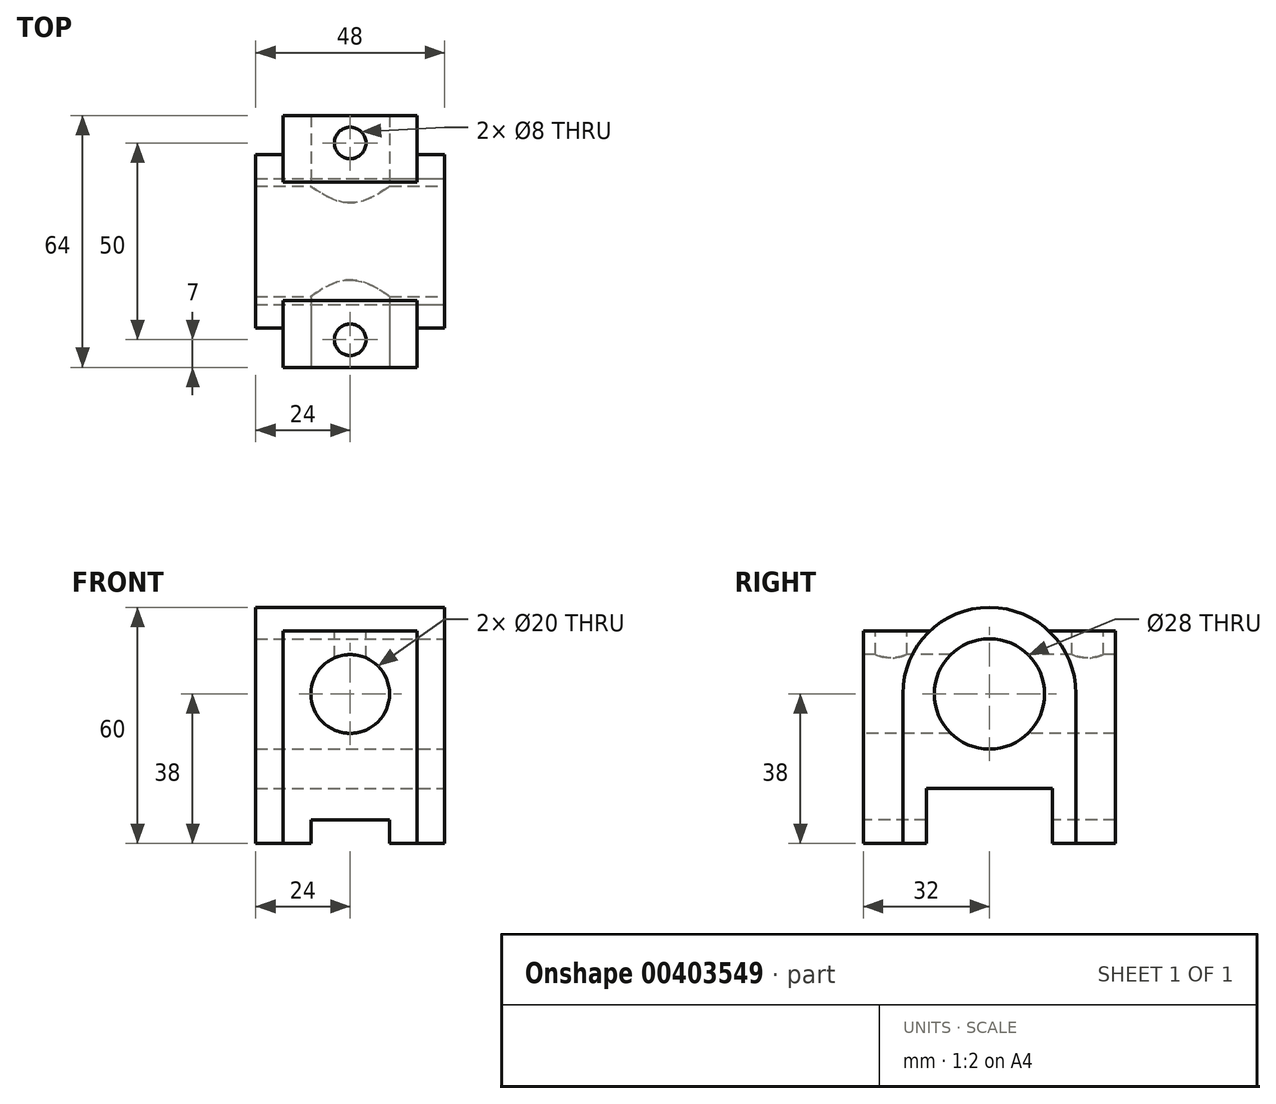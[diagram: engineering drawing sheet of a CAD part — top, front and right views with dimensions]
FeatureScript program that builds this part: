
annotation { "Feature Type Name" : "Feature", "Feature Type Description" : "" }
export const myFeature = defineFeature(function(context is Context, id is Id, definition is map)
    precondition{}
    {
        {
            var Q0;
            Q0=qCreatedBy(makeId("Right.planeOp"),FACE);
            var sketch = newSketch(context, id + "F0", { "sketchPlane" : qUnion([Q0])});
            skLineSegment(sketch, "E0.bottom", {"start": v(-22, 30) * mm, "end": v(22, 30) * mm});
            skLineSegment(sketch, "E0.top", {"start": v(-22, -30) * mm, "end": v(22, -30) * mm});
            skLineSegment(sketch, "E0.left", {"start": v(-22, 30) * mm, "end": v(-22, -30) * mm});
            skLineSegment(sketch, "E0.right", {"start": v(22, 30) * mm, "end": v(22, -30) * mm});
            skPoint(sketch, "E0.middle", {"position": v(0, 0) * mm});
            skSolve(sketch);
        }
        {
            var Q0;
            Q0 = qSketchRegion(id + "F0", true);
            extrude(context, id + "F1", {"entities" : qUnion([Q0]), "endBound" : BoundingType.SYMMETRIC, "depth" : 48 * mm});
        }
        {
            var Q0;
            Q0=makeQuery(id+"F1.opExtrude","SWEPT_EDGE",EDGE,{"disambiguationData":[OSD([sQuery(id+"F0.wireOp",EDGE,"E0.bottom"),sQuery(id+"F0.wireOp",EDGE,"E0.left")])]});
            var Q1;
            Q1=makeQuery(id+"F1.opExtrude","SWEPT_EDGE",EDGE,{"disambiguationData":[OSD([sQuery(id+"F0.wireOp",EDGE,"E0.bottom"),sQuery(id+"F0.wireOp",EDGE,"E0.right")])]});
            fillet(context, id + "F2", {"entities" : qUnion([Q0, Q1]), "radius" : 22 * mm, "tangentPropagation" : true, "allowEdgeOverflow" : false});
        }
        {
            var Q0;
            Q0=makeQuery(id+"F1.opExtrude","SWEPT_FACE",FACE,{"disambiguationData":[OSD([sQuery(id+"F0.wireOp",EDGE,"E0.left")])]});
            var sketch = newSketch(context, id + "F3", { "sketchPlane" : qUnion([Q0])});
            skLineSegment(sketch, "E1.bottom", {"start": v(-17, -30) * mm, "end": v(17, -30) * mm});
            skLineSegment(sketch, "E1.top", {"start": v(-17, 24) * mm, "end": v(17, 24) * mm});
            skLineSegment(sketch, "E1.left", {"start": v(-17, -30) * mm, "end": v(-17, 24) * mm});
            skLineSegment(sketch, "E1.right", {"start": v(17, -30) * mm, "end": v(17, 24) * mm});
            skSolve(sketch);
        }
        {
            var Q0;
            Q0 = qSketchRegion(id + "F3", true);
            extrude(context, id + "F4", {"entities" : qUnion([Q0]), "operationType" : NewBodyOperationType.ADD, "depth" : 10 * mm, "hasSecondDirection" : true, "secondDirectionOppositeDirection" : true, "secondDirectionDepth" : 54 * mm});
        }
        {
            var Q0;
            Q0=makeQuery(id+"F1.opExtrude","CAP_FACE",FACE,{"disambiguationData":[OSD([sQuery(id+"F0.wireOp",EDGE,"E0.bottom"),sQuery(id+"F0.wireOp",EDGE,"E0.top"),sQuery(id+"F0.wireOp",EDGE,"E0.left"),sQuery(id+"F0.wireOp",EDGE,"E0.right")])],"isStart":false});
            var sketch = newSketch(context, id + "F5", { "sketchPlane" : qUnion([Q0])});
            skCircle(sketch, "E2", {"center": v(0, 8) * mm, "radius": 14 * mm});
            skLineSegment(sketch, "E3.bottom", {"start": v(-16, -16) * mm, "end": v(16, -16) * mm});
            skLineSegment(sketch, "E3.top", {"start": v(-16, -30) * mm, "end": v(16, -30) * mm});
            skLineSegment(sketch, "E3.left", {"start": v(-16, -16) * mm, "end": v(-16, -30) * mm});
            skLineSegment(sketch, "E3.right", {"start": v(16, -16) * mm, "end": v(16, -30) * mm});
            skSolve(sketch);
        }
        {
            var Q0;
            Q0 = qSketchRegion(id + "F5", true);
            extrude(context, id + "F6", {"entities" : qUnion([Q0]), "operationType" : NewBodyOperationType.REMOVE, "endBound" : BoundingType.THROUGH_ALL, "oppositeDirection" : true, "depth" : 25 * mm});
        }
        {
            var Q0;
            {var subQ0=sQuery(id+"F3.wireOp",EDGE,"E1.right");var subQ1=sQuery(id+"F3.wireOp",EDGE,"E1.left");var subQ2=sQuery(id+"F3.wireOp",EDGE,"E1.top");Q0=makeQuery(id+"F4.boolean.opBoolean","SPLIT",FACE,{"disambiguationData":[TD([makeQuery(id+"F4.opExtrude","CAP_FACE",FACE,{"disambiguationData":[OSD([sQuery(id+"F3.wireOp",EDGE,"E1.bottom"),subQ2,subQ1,subQ0])],"isStart":false})])],"derivedFrom":makeQuery(id+"F4.opExtrude","SWEPT_FACE",FACE,{"disambiguationData":[OSD([subQ2])]})});}
            var sketch = newSketch(context, id + "F7", { "sketchPlane" : qUnion([Q0])});
            skCircle(sketch, "E4", {"center": v(0, -25) * mm, "radius": 4 * mm});
            skPoint(sketch, "E4.centerSnap0", {"position": v(-17, -23.55) * mm});
            skPoint(sketch, "E4.centerSnap1", {"position": v(0, -32) * mm});
            skCircle(sketch, "E5", {"center": v(0, 25) * mm, "radius": 4 * mm});
            skSolve(sketch);
        }
        {
            var Q0;
            Q0=makeQuery(id+"F4.opExtrude","CAP_FACE",FACE,{"disambiguationData":[OSD([sQuery(id+"F3.wireOp",EDGE,"E1.bottom"),sQuery(id+"F3.wireOp",EDGE,"E1.top"),sQuery(id+"F3.wireOp",EDGE,"E1.left"),sQuery(id+"F3.wireOp",EDGE,"E1.right")])],"isStart":false});
            var sketch = newSketch(context, id + "F8", { "sketchPlane" : qUnion([Q0])});
            skCircle(sketch, "E6", {"center": v(0, 8) * mm, "radius": 10 * mm});
            skLineSegment(sketch, "E7.bottom", {"start": v(-10, -24) * mm, "end": v(10, -24) * mm});
            skLineSegment(sketch, "E7.top", {"start": v(-10, -30) * mm, "end": v(10, -30) * mm});
            skLineSegment(sketch, "E7.left", {"start": v(-10, -24) * mm, "end": v(-10, -30) * mm});
            skLineSegment(sketch, "E7.right", {"start": v(10, -24) * mm, "end": v(10, -30) * mm});
            skSolve(sketch);
        }
        {
            var Q0;
            Q0 = qSketchRegion(id + "F8", true);
            extrude(context, id + "F9", {"entities" : qUnion([Q0]), "operationType" : NewBodyOperationType.REMOVE, "endBound" : BoundingType.THROUGH_ALL, "oppositeDirection" : true, "depth" : 25 * mm});
        }
        {
            var Q0;
            Q0 = qSketchRegion(id + "F7", true);
            var Q1;
            Q1=makeQuery(id+"F9.boolean.opBoolean","COPY",FACE,{"disambiguationData":[TD([makeQuery(id+"F4.opExtrude","CAP_FACE",FACE,{"disambiguationData":[OSD([sQuery(id+"F3.wireOp",EDGE,"E1.bottom"),sQuery(id+"F3.wireOp",EDGE,"E1.top"),sQuery(id+"F3.wireOp",EDGE,"E1.left"),sQuery(id+"F3.wireOp",EDGE,"E1.right")])],"isStart":false})])],"derivedFrom":makeQuery(id+"F9.opExtrude","SWEPT_FACE",FACE,{"disambiguationData":[OSD([sQuery(id+"F8.wireOp",EDGE,"E6")])]})});
            extrude(context, id + "F10", {"entities" : qUnion([Q0]), "operationType" : NewBodyOperationType.REMOVE, "endBound" : BoundingType.UP_TO_SURFACE, "oppositeDirection" : true, "endBoundEntityFace" : qUnion([Q1]), "depth" : 25 * mm});
        }
    });
